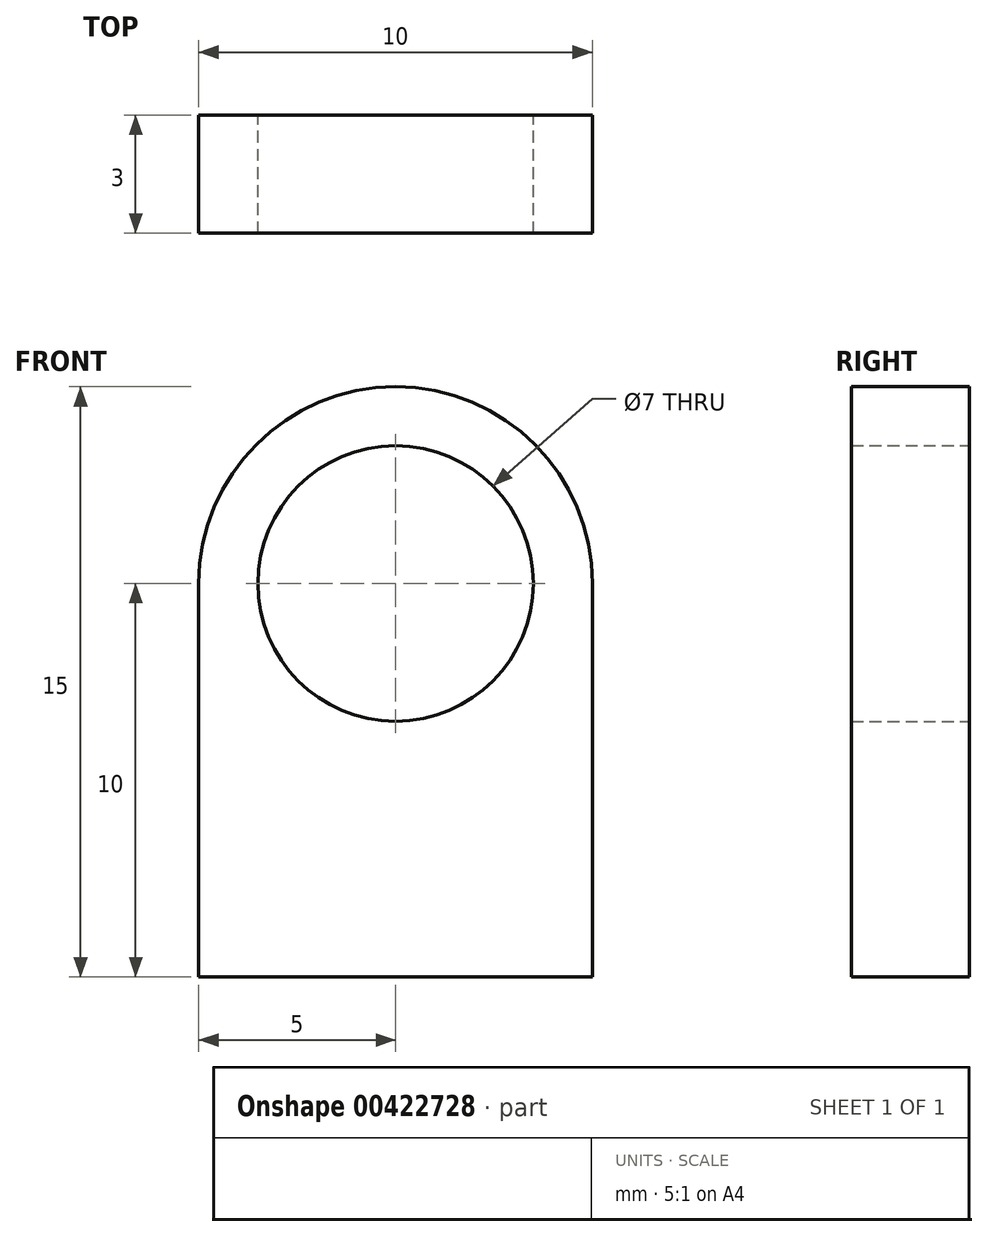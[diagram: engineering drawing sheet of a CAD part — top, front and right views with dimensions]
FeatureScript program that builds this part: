
annotation { "Feature Type Name" : "Feature", "Feature Type Description" : "" }
export const myFeature = defineFeature(function(context is Context, id is Id, definition is map)
    precondition{}
    {
        {
            var Q0;
            Q0=qCreatedBy(makeId("Front.planeOp"),FACE);
            var sketch = newSketch(context, id + "F0", { "sketchPlane" : qUnion([Q0])});
            skCircle(sketch, "E0", {"center": v(0, 0) * mm, "radius": 3.5 * mm});
            skCircle(sketch, "E1", {"center": v(0, 0) * mm, "radius": 5 * mm});
            skLineSegment(sketch, "E2.top", {"start": v(-5, -10) * mm, "end": v(5, -10) * mm});
            skLineSegment(sketch, "E2.left", {"start": v(-5, 0) * mm, "end": v(-5, -10) * mm});
            skLineSegment(sketch, "E2.right", {"start": v(5, 0) * mm, "end": v(5, -10) * mm});
            skSolve(sketch);
        }
        {
            var Q0;
            Q0 = qSketchRegion(id + "F0", true);
            extrude(context, id + "F1", {"entities" : qUnion([Q0]), "endBound" : BoundingType.SYMMETRIC, "depth" : 3 * mm});
        }
    });
